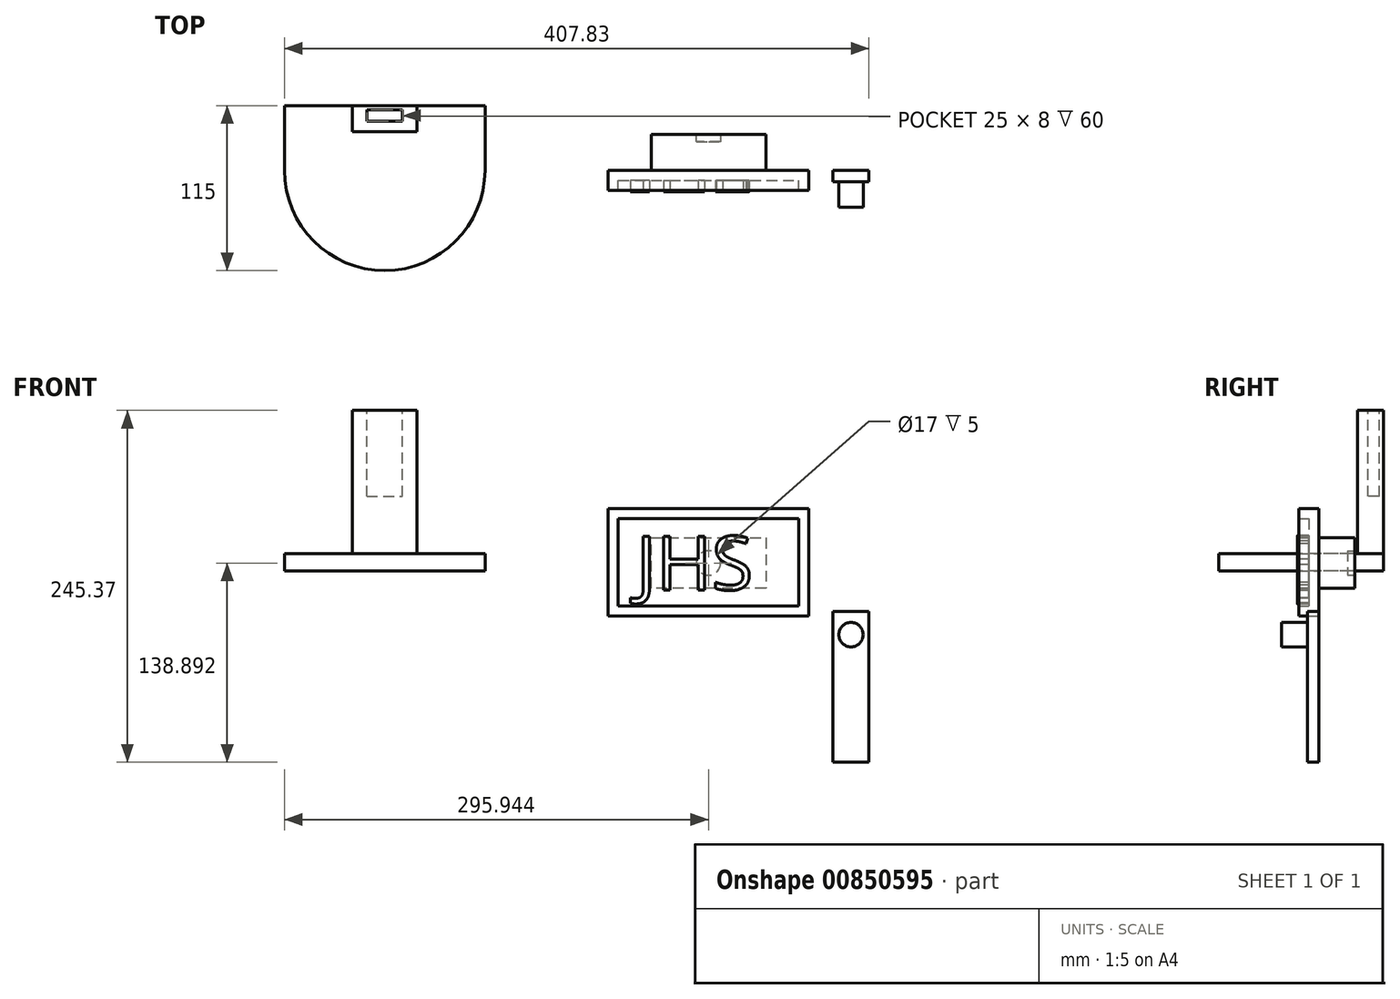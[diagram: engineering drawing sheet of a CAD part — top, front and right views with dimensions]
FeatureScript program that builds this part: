
annotation { "Feature Type Name" : "Feature", "Feature Type Description" : "" }
export const myFeature = defineFeature(function(context is Context, id is Id, definition is map)
    precondition{}
    {
        {
            var Q0;
            Q0=qCreatedBy(makeId("Front.planeOp"),FACE);
            var sketch = newSketch(context, id + "F0", { "sketchPlane" : qUnion([Q0])});
            skLineSegment(sketch, "E0.bottom", {"start": v(-102.96, 43.38) * mm, "end": v(37.04, 43.38) * mm});
            skLineSegment(sketch, "E0.top", {"start": v(-102.96, -31.62) * mm, "end": v(37.04, -31.62) * mm});
            skLineSegment(sketch, "E0.left", {"start": v(-102.96, 43.38) * mm, "end": v(-102.96, -31.62) * mm});
            skLineSegment(sketch, "E0.right", {"start": v(37.04, 43.38) * mm, "end": v(37.04, -31.62) * mm});
            skSolve(sketch);
        }
        {
            var Q0;
            Q0=makeQuery(id+"F0.imprint","IMPRINT",FACE,{"disambiguationData":[TD([[makeQuery(id+"F0.imprint","IMPRINT",EDGE,{"derivedFrom":sQuery(id+"F0.wireOp",EDGE,"E0.bottom")}),-1.0]])]});
            extrude(context, id + "F1", {"entities" : qUnion([Q0]), "depth" : 14 * mm, "offsetDistance" : 25 * mm});
        }
        {
            var Q0;
            Q0=makeQuery(id+"F1.opExtrude","CAP_FACE",FACE,{"disambiguationData":[OSD([sQuery(id+"F0.wireOp",EDGE,"E0.bottom"),sQuery(id+"F0.wireOp",EDGE,"E0.top"),sQuery(id+"F0.wireOp",EDGE,"E0.left"),sQuery(id+"F0.wireOp",EDGE,"E0.right")])],"isStart":false});
            shell(context, id + "F2", {"entities" : qUnion([Q0]), "thickness" : 7 * mm});
        }
        {
            var Q0;
            Q0=makeQuery(id+"F2.opShell","OFFSET_FACE",FACE,{"disambiguationData":[OSD([sQuery(id+"F0.wireOp",EDGE,"E0.bottom"),sQuery(id+"F0.wireOp",EDGE,"E0.top"),sQuery(id+"F0.wireOp",EDGE,"E0.left"),sQuery(id+"F0.wireOp",EDGE,"E0.right")])]});
            cPlane(context, id + "F3", {"entities" : qUnion([Q0]), "cplaneType" : CPlaneType.OFFSET, "offset" : 8 * mm, "width" : 150 * mm, "height" : 150 * mm});
        }
        {
            var Q0;
            Q0=qCreatedBy(id+"F3.planeOp",FACE);
            var sketch = newSketch(context, id + "F4", { "sketchPlane" : qUnion([Q0])});
            skText(sketch, "E1", { "text": "JHS", "fontName": "OpenSans-Regular.ttf"});
            const initialGuessF4  = {"E1": [-0.08345, -0.01323, 1, 0, 0.03775]};
            skSetInitialGuess(sketch, initialGuessF4);
            skSolve(sketch);
        }
        {
            var Q0;
            Q0 = qSketchRegion(id + "F4", true);
            extrude(context, id + "F5", {"entities" : qUnion([Q0]), "operationType" : NewBodyOperationType.ADD, "endBound" : BoundingType.UP_TO_NEXT, "oppositeDirection" : true, "depth" : 25 * mm, "offsetDistance" : 25 * mm});
        }
        {
            var Q0;
            Q0=makeQuery(id+"F1.opExtrude","CAP_FACE",FACE,{"disambiguationData":[OSD([sQuery(id+"F0.wireOp",EDGE,"E0.bottom"),sQuery(id+"F0.wireOp",EDGE,"E0.top"),sQuery(id+"F0.wireOp",EDGE,"E0.left"),sQuery(id+"F0.wireOp",EDGE,"E0.right")])],"isStart":true});
            var sketch = newSketch(context, id + "F6", { "sketchPlane" : qUnion([Q0])});
            skLineSegment(sketch, "E2", {"start": v(-37.04, 43.38) * mm, "end": v(32.96, 43.38) * mm});
            skLineSegment(sketch, "E3", {"start": v(32.96, 23.02) * mm, "end": v(-7.04, 23.02) * mm});
            skLineSegment(sketch, "E4", {"start": v(-7.04, 23.02) * mm, "end": v(-7.04, -11.98) * mm});
            skLineSegment(sketch, "E5", {"start": v(-7.04, -11.98) * mm, "end": v(72.96, -11.98) * mm});
            skLineSegment(sketch, "E6", {"start": v(72.96, -11.98) * mm, "end": v(72.96, 23.02) * mm});
            skLineSegment(sketch, "E7", {"start": v(72.96, 23.02) * mm, "end": v(32.96, 23.02) * mm});
            skSolve(sketch);
        }
        {
            var Q0;
            Q0=makeQuery(id+"F6.imprint","IMPRINT",FACE,{"disambiguationData":[TD([[makeQuery(id+"F6.imprint","IMPRINT",EDGE,{"derivedFrom":sQuery(id+"F6.wireOp",EDGE,"E3")}),1.0]])]});
            extrude(context, id + "F7", {"entities" : qUnion([Q0]), "operationType" : NewBodyOperationType.ADD, "depth" : 25 * mm, "offsetDistance" : 25 * mm});
        }
        {
            var Q0;
            Q0=makeQuery(id+"F7.opExtrude","CAP_FACE",FACE,{"disambiguationData":[OSD([sQuery(id+"F6.wireOp",EDGE,"E3"),sQuery(id+"F6.wireOp",EDGE,"E4"),sQuery(id+"F6.wireOp",EDGE,"E5"),sQuery(id+"F6.wireOp",EDGE,"E6"),sQuery(id+"F6.wireOp",EDGE,"E7")])],"isStart":false});
            var sketch = newSketch(context, id + "F8", { "sketchPlane" : qUnion([Q0])});
            skCircle(sketch, "E8", {"center": v(32.96, 5.52) * mm, "radius": 8.5 * mm});
            skPoint(sketch, "E9.orphan", {"position": v(32.96, 23.02) * mm});
            skPoint(sketch, "E10.end.orphan", {"position": v(32.96, -11.98) * mm});
            skSolve(sketch);
        }
        {
            var Q0;
            Q0=makeQuery(id+"F8.imprint","IMPRINT",FACE,{"disambiguationData":[TD([[makeQuery(id+"F8.imprint","IMPRINT",EDGE,{"derivedFrom":sQuery(id+"F8.wireOp",EDGE,"E8")}),1.0]])]});
            extrude(context, id + "F9", {"entities" : qUnion([Q0]), "operationType" : NewBodyOperationType.REMOVE, "oppositeDirection" : true, "depth" : 5 * mm, "offsetDistance" : 25 * mm});
        }
        {
            var Q0;
            Q0=qCreatedBy(makeId("Front.planeOp"),FACE);
            var sketch = newSketch(context, id + "F10", { "sketchPlane" : qUnion([Q0])});
            skLineSegment(sketch, "E11.bottom", {"start": v(53.93, -28.37) * mm, "end": v(78.93, -28.37) * mm});
            skLineSegment(sketch, "E11.top", {"start": v(53.93, -133.37) * mm, "end": v(78.93, -133.37) * mm});
            skLineSegment(sketch, "E11.left", {"start": v(53.93, -28.37) * mm, "end": v(53.93, -133.37) * mm});
            skLineSegment(sketch, "E11.right", {"start": v(78.93, -28.37) * mm, "end": v(78.93, -133.37) * mm});
            skSolve(sketch);
        }
        {
            var Q0;
            Q0=makeQuery(id+"F10.imprint","IMPRINT",FACE,{"disambiguationData":[TD([[makeQuery(id+"F10.imprint","IMPRINT",EDGE,{"derivedFrom":sQuery(id+"F10.wireOp",EDGE,"E11.bottom")}),-1.0]])]});
            extrude(context, id + "F11", {"entities" : qUnion([Q0]), "depth" : 8 * mm, "offsetDistance" : 25 * mm});
        }
        {
            var Q0;
            Q0=makeQuery(id+"F11.opExtrude","CAP_FACE",FACE,{"disambiguationData":[OSD([sQuery(id+"F10.wireOp",EDGE,"E11.bottom"),sQuery(id+"F10.wireOp",EDGE,"E11.top"),sQuery(id+"F10.wireOp",EDGE,"E11.left"),sQuery(id+"F10.wireOp",EDGE,"E11.right")])],"isStart":false});
            var sketch = newSketch(context, id + "F12", { "sketchPlane" : qUnion([Q0])});
            skCircle(sketch, "E12", {"center": v(66.43, -44.46) * mm, "radius": 8.5 * mm});
            skPoint(sketch, "E13.orphan", {"position": v(66.43, -28.37) * mm});
            skSolve(sketch);
        }
        {
            var Q0;
            Q0=makeQuery(id+"F12.imprint","IMPRINT",FACE,{"disambiguationData":[TD([[makeQuery(id+"F12.imprint","IMPRINT",EDGE,{"derivedFrom":sQuery(id+"F12.wireOp",EDGE,"E12")}),1.0]])]});
            extrude(context, id + "F13", {"entities" : qUnion([Q0]), "operationType" : NewBodyOperationType.ADD, "depth" : 18 * mm, "offsetDistance" : 25 * mm});
        }
        {
            var Q0;
            Q0=qCreatedBy(makeId("Top.planeOp"),FACE);
            var sketch = newSketch(context, id + "F14", { "sketchPlane" : qUnion([Q0])});
            skLineSegment(sketch, "E14.bottom", {"start": v(-328.9, 45) * mm, "end": v(-188.9, 45) * mm});
            skLineSegment(sketch, "E14.left", {"start": v(-328.9, 45) * mm, "end": v(-328.9, 0) * mm});
            skLineSegment(sketch, "E14.right", {"start": v(-188.9, 45) * mm, "end": v(-188.9, 0) * mm});
            skArc(sketch, "E15", {"start": v(-328.9, 0) * mm, "mid": v(-258.9, -70) * mm, "end": v(-188.9, 0) * mm});
            skSolve(sketch);
        }
        {
            var Q0;
            Q0 = qSketchRegion(id + "F14", true);
            extrude(context, id + "F15", {"entities" : qUnion([Q0]), "depth" : 12 * mm, "offsetDistance" : 25 * mm});
        }
        {
            var Q0;
            Q0=makeQuery(id+"F15.opExtrude","CAP_FACE",FACE,{"disambiguationData":[OSD([sQuery(id+"F14.wireOp",EDGE,"E14.bottom"),sQuery(id+"F14.wireOp",EDGE,"E14.left"),sQuery(id+"F14.wireOp",EDGE,"E14.right"),sQuery(id+"F14.wireOp",EDGE,"E15")])],"isStart":false});
            var sketch = newSketch(context, id + "F16", { "sketchPlane" : qUnion([Q0])});
            skLineSegment(sketch, "E16", {"start": v(-258.9, 45) * mm, "end": v(-281.4, 45) * mm});
            skLineSegment(sketch, "E17", {"start": v(-281.4, 45) * mm, "end": v(-281.4, 27) * mm});
            skLineSegment(sketch, "E18", {"start": v(-281.4, 27) * mm, "end": v(-236.4, 27) * mm});
            skLineSegment(sketch, "E19", {"start": v(-236.4, 27) * mm, "end": v(-236.4, 45) * mm});
            skSolve(sketch);
        }
        {
            var Q0;
            {var subQ1=sQuery(id+"F16.wireOp",EDGE,"E16");Q0=makeQuery(id+"F16.imprint","IMPRINT",FACE,{"disambiguationData":[TD([[makeQuery(id+"F16.imprint","IMPRINT",EDGE,{"derivedFrom":subQ1}),-1.0]])]});}
            extrude(context, id + "F17", {"entities" : qUnion([Q0]), "operationType" : NewBodyOperationType.ADD, "depth" : 100 * mm, "offsetDistance" : 25 * mm});
        }
        {
            var Q0;
            Q0=makeQuery(id+"F17.opExtrude","CAP_FACE",FACE,{"disambiguationData":[OSD([sQuery(id+"F14.wireOp",EDGE,"E14.bottom"),sQuery(id+"F16.wireOp",EDGE,"E16"),sQuery(id+"F16.wireOp",EDGE,"E17"),sQuery(id+"F16.wireOp",EDGE,"E18"),sQuery(id+"F16.wireOp",EDGE,"E19")])],"isStart":false});
            var sketch = newSketch(context, id + "F18", { "sketchPlane" : qUnion([Q0])});
            skLineSegment(sketch, "E20", {"start": v(-258.9, 42.09) * mm, "end": v(-271.4, 42.09) * mm});
            skLineSegment(sketch, "E21", {"start": v(-258.9, 42.09) * mm, "end": v(-246.4, 42.09) * mm});
            skLineSegment(sketch, "E22", {"start": v(-271.4, 42.09) * mm, "end": v(-271.4, 34.09) * mm});
            skLineSegment(sketch, "E23", {"start": v(-271.4, 34.09) * mm, "end": v(-246.4, 34.09) * mm});
            skLineSegment(sketch, "E24", {"start": v(-246.4, 34.09) * mm, "end": v(-246.4, 42.09) * mm});
            skPoint(sketch, "E25.start.orphan", {"position": v(-258.9, 45) * mm});
            skSolve(sketch);
        }
        {
            var Q0;
            Q0=makeQuery(id+"F18.imprint","IMPRINT",FACE,{"disambiguationData":[TD([[makeQuery(id+"F18.imprint","IMPRINT",EDGE,{"derivedFrom":sQuery(id+"F18.wireOp",EDGE,"E20")}),1.0]])]});
            extrude(context, id + "F19", {"entities" : qUnion([Q0]), "operationType" : NewBodyOperationType.REMOVE, "oppositeDirection" : true, "depth" : 60 * mm, "offsetDistance" : 25 * mm});
        }
    });
